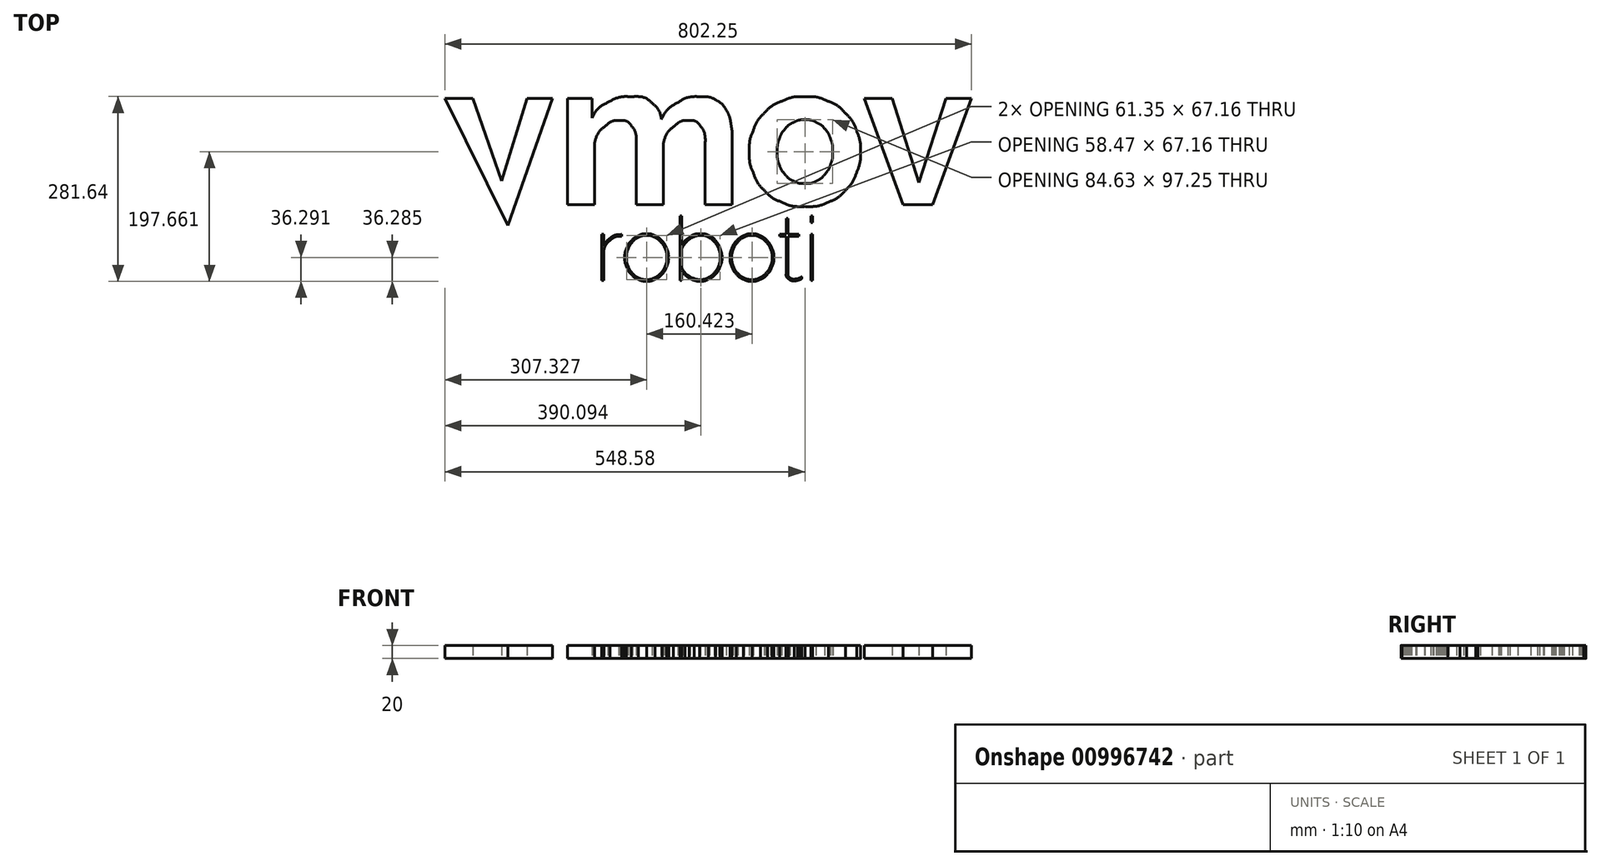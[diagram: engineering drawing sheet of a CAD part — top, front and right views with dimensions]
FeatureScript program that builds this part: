
annotation { "Feature Type Name" : "Feature", "Feature Type Description" : "" }
export const myFeature = defineFeature(function(context is Context, id is Id, definition is map)
    precondition{}
    {
        {
            var Q0;
            Q0=qCreatedBy(makeId("Top.planeOp"),FACE);
            var sketch = newSketch(context, id + "F0", { "sketchPlane" : qUnion([Q0])});
            skLineSegment(sketch, "E0", {"start": v(-278.2, 23.95) * mm, "end": v(-293.61, -1.95) * mm});
            skLineSegment(sketch, "E1", {"start": v(-293.61, -1.95) * mm, "end": v(-278.2, 23.95) * mm});
            skLineSegment(sketch, "E2", {"start": v(-178, 93.62) * mm, "end": v(-161.36, 118.6) * mm});
            skLineSegment(sketch, "E3", {"start": v(-161.36, 118.6) * mm, "end": v(-178, 93.62) * mm});
            skLineSegment(sketch, "E4", {"start": v(-493.33, 15.32) * mm, "end": v(-528.78, 25.18) * mm});
            skLineSegment(sketch, "E5", {"start": v(-528.78, 25.18) * mm, "end": v(-493.33, 15.32) * mm});
            skLineSegment(sketch, "E6", {"start": v(-609.86, 43.68) * mm, "end": v(-485, 43.68) * mm});
            skLineSegment(sketch, "E7", {"start": v(-485, 43.68) * mm, "end": v(-609.86, 43.68) * mm});
            skLineSegment(sketch, "E8", {"start": v(-460.77, 119.82) * mm, "end": v(-448.13, 93.62) * mm});
            skLineSegment(sketch, "E9", {"start": v(-448.13, 93.62) * mm, "end": v(-460.77, 119.82) * mm});
            skLineSegment(sketch, "E10", {"start": v(-361.5, 78.52) * mm, "end": v(-361.5, 69.26) * mm});
            skLineSegment(sketch, "E11", {"start": v(-361.5, 69.26) * mm, "end": v(-361.5, 78.52) * mm});
            skLineSegment(sketch, "E12", {"start": v(-355.33, 2.06) * mm, "end": v(-354.41, -6.88) * mm});
            skLineSegment(sketch, "E13", {"start": v(-354.41, -6.88) * mm, "end": v(-355.33, 2.06) * mm});
            skLineSegment(sketch, "E14", {"start": v(-310.33, -23.84) * mm, "end": v(-310.33, 11.3) * mm});
            skLineSegment(sketch, "E15", {"start": v(-310.33, 11.3) * mm, "end": v(-310.33, -23.84) * mm});
            skLineSegment(sketch, "E16", {"start": v(-320.2, 23.64) * mm, "end": v(-320.2, 73.89) * mm});
            skLineSegment(sketch, "E17", {"start": v(-320.2, 73.89) * mm, "end": v(-320.2, 23.64) * mm});
            skLineSegment(sketch, "E18", {"start": v(75.43, 107.8) * mm, "end": v(75.43, 137.7) * mm});
            skLineSegment(sketch, "E19", {"start": v(75.43, 137.7) * mm, "end": v(38.13, 137.7) * mm});
            skLineSegment(sketch, "E20", {"start": v(38.13, 137.7) * mm, "end": v(38.13, -23.84) * mm});
            skLineSegment(sketch, "E21", {"start": v(38.13, -23.84) * mm, "end": v(79.44, -23.84) * mm});
            skLineSegment(sketch, "E22", {"start": v(79.44, -23.84) * mm, "end": v(79.44, 70.5) * mm});
            skLineSegment(sketch, "E23", {"start": v(79.44, 70.5) * mm, "end": v(75.43, 107.8) * mm});
            skLineSegment(sketch, "E24", {"start": v(142.94, 66.8) * mm, "end": v(142.94, -23.84) * mm});
            skLineSegment(sketch, "E25", {"start": v(142.94, -23.84) * mm, "end": v(184.25, -23.84) * mm});
            skLineSegment(sketch, "E26", {"start": v(184.25, -23.84) * mm, "end": v(184.25, 70.19) * mm});
            skLineSegment(sketch, "E27", {"start": v(184.25, 70.19) * mm, "end": v(142.94, 66.8) * mm});
            skLineSegment(sketch, "E28", {"start": v(247.76, 66.8) * mm, "end": v(247.76, -23.84) * mm});
            skLineSegment(sketch, "E29", {"start": v(247.76, -23.84) * mm, "end": v(289.07, -23.84) * mm});
            skLineSegment(sketch, "E30", {"start": v(289.07, -23.84) * mm, "end": v(289.07, 76.98) * mm});
            skLineSegment(sketch, "E31", {"start": v(289.07, 76.98) * mm, "end": v(247.76, 66.8) * mm});
            skLineSegment(sketch, "E32", {"start": v(-148.62, 137.7) * mm, "end": v(-84.8, -23.84) * mm});
            skLineSegment(sketch, "E33", {"start": v(-84.8, -23.84) * mm, "end": v(-148.62, 137.7) * mm});
            skLineSegment(sketch, "E34", {"start": v(-128.27, -55.28) * mm, "end": v(-128.27, -91.04) * mm});
            skLineSegment(sketch, "E35", {"start": v(-128.27, -91.04) * mm, "end": v(-128.27, -55.28) * mm});
            skLineSegment(sketch, "E36", {"start": v(-52.44, -55.9) * mm, "end": v(15.39, 137.7) * mm});
            skLineSegment(sketch, "E37", {"start": v(15.39, 137.7) * mm, "end": v(-23.46, 137.7) * mm});
            skLineSegment(sketch, "E38", {"start": v(-23.46, 137.7) * mm, "end": v(-62.3, 11.92) * mm});
            skLineSegment(sketch, "E39", {"start": v(-62.3, 11.92) * mm, "end": v(-106.08, 137.7) * mm});
            skLineSegment(sketch, "E40", {"start": v(-106.08, 137.7) * mm, "end": v(-148.62, 137.7) * mm});
            skLineSegment(sketch, "E41", {"start": v(-148.62, 137.7) * mm, "end": v(-52.44, -55.9) * mm});
            skLineSegment(sketch, "E42", {"start": v(489.94, 137.7) * mm, "end": v(549.44, -23.84) * mm});
            skLineSegment(sketch, "E43", {"start": v(549.44, -23.84) * mm, "end": v(594.14, -23.84) * mm});
            skLineSegment(sketch, "E44", {"start": v(594.14, -23.84) * mm, "end": v(653.63, 137.7) * mm});
            skLineSegment(sketch, "E45", {"start": v(653.63, 137.7) * mm, "end": v(614.8, 137.7) * mm});
            skLineSegment(sketch, "E46", {"start": v(614.8, 137.7) * mm, "end": v(573.48, 9.77) * mm});
            skLineSegment(sketch, "E47", {"start": v(573.48, 9.77) * mm, "end": v(532.48, 137.7) * mm});
            skLineSegment(sketch, "E48", {"start": v(532.48, 137.7) * mm, "end": v(489.94, 137.7) * mm});
            skLineSegment(sketch, "E49", {"start": v(-526.62, 70.5) * mm, "end": v(-610.47, 70.5) * mm});
            skLineSegment(sketch, "E50", {"start": v(-610.47, 70.5) * mm, "end": v(-526.62, 70.5) * mm});
            skLineSegment(sketch, "E51", {"start": v(-361.5, 47.07) * mm, "end": v(-361.5, 28.57) * mm});
            skLineSegment(sketch, "E52", {"start": v(-361.5, 28.57) * mm, "end": v(-361.5, 47.07) * mm});
            skLineSegment(sketch, "E53", {"start": v(209.55, -40.98) * mm, "end": v(209.55, -139.44) * mm});
            skLineSegment(sketch, "E54", {"start": v(209.55, -139.44) * mm, "end": v(212.24, -139.44) * mm});
            skLineSegment(sketch, "E55", {"start": v(212.24, -139.44) * mm, "end": v(212.24, -124.87) * mm});
            skLineSegment(sketch, "E56", {"start": v(212.24, -124.87) * mm, "end": v(209.55, -40.98) * mm});
            skLineSegment(sketch, "E57", {"start": v(212.24, -85.76) * mm, "end": v(212.24, -40.98) * mm});
            skLineSegment(sketch, "E58", {"start": v(212.24, -40.98) * mm, "end": v(209.55, -40.98) * mm});
            skLineSegment(sketch, "E59", {"start": v(209.55, -40.98) * mm, "end": v(212.24, -85.76) * mm});
            skLineSegment(sketch, "E60", {"start": v(408.7, -40.98) * mm, "end": v(408.7, -51.37) * mm});
            skLineSegment(sketch, "E61", {"start": v(408.7, -51.37) * mm, "end": v(411.4, -51.37) * mm});
            skLineSegment(sketch, "E62", {"start": v(411.4, -51.37) * mm, "end": v(411.4, -40.98) * mm});
            skLineSegment(sketch, "E63", {"start": v(411.4, -40.98) * mm, "end": v(408.7, -40.98) * mm});
            skLineSegment(sketch, "E64", {"start": v(371.21, -45.03) * mm, "end": v(371.21, -69.44) * mm});
            skLineSegment(sketch, "E65", {"start": v(371.21, -69.44) * mm, "end": v(361.1, -69.44) * mm});
            skLineSegment(sketch, "E66", {"start": v(361.1, -69.44) * mm, "end": v(361.1, -72.14) * mm});
            skLineSegment(sketch, "E67", {"start": v(361.1, -72.14) * mm, "end": v(371.21, -72.14) * mm});
            skLineSegment(sketch, "E68", {"start": v(371.21, -72.14) * mm, "end": v(371.21, -129.32) * mm});
            skLineSegment(sketch, "E69", {"start": v(371.21, -129.32) * mm, "end": v(371.21, -45.03) * mm});
            skLineSegment(sketch, "E70", {"start": v(395.08, -136.87) * mm, "end": v(396.16, -136.2) * mm});
            skLineSegment(sketch, "E71", {"start": v(396.16, -136.2) * mm, "end": v(394.68, -134.04) * mm});
            skLineSegment(sketch, "E72", {"start": v(394.68, -134.04) * mm, "end": v(395.08, -136.87) * mm});
            skLineSegment(sketch, "E73", {"start": v(373.9, -129.32) * mm, "end": v(373.9, -72.14) * mm});
            skLineSegment(sketch, "E74", {"start": v(373.9, -72.14) * mm, "end": v(390.77, -72.14) * mm});
            skLineSegment(sketch, "E75", {"start": v(390.77, -72.14) * mm, "end": v(390.77, -69.44) * mm});
            skLineSegment(sketch, "E76", {"start": v(390.77, -69.44) * mm, "end": v(373.9, -69.44) * mm});
            skLineSegment(sketch, "E77", {"start": v(373.9, -69.44) * mm, "end": v(373.9, -45.03) * mm});
            skLineSegment(sketch, "E78", {"start": v(373.9, -45.03) * mm, "end": v(371.21, -45.03) * mm});
            skLineSegment(sketch, "E79", {"start": v(371.21, -45.03) * mm, "end": v(373.9, -129.32) * mm});
            skLineSegment(sketch, "E80", {"start": v(489.82, -124.2) * mm, "end": v(487.12, -123.4) * mm});
            skLineSegment(sketch, "E81", {"start": v(487.12, -123.4) * mm, "end": v(489.82, -124.2) * mm});
            skLineSegment(sketch, "E82", {"start": v(486.18, -84.95) * mm, "end": v(488.88, -84) * mm});
            skLineSegment(sketch, "E83", {"start": v(488.88, -84) * mm, "end": v(486.18, -84.95) * mm});
            skLineSegment(sketch, "E84", {"start": v(502.11, -127.7) * mm, "end": v(500.09, -129.46) * mm});
            skLineSegment(sketch, "E85", {"start": v(500.09, -129.46) * mm, "end": v(502.11, -127.7) * mm});
            skLineSegment(sketch, "E86", {"start": v(548.37, -79.56) * mm, "end": v(550.8, -78.48) * mm});
            skLineSegment(sketch, "E87", {"start": v(550.8, -78.48) * mm, "end": v(548.37, -79.56) * mm});
            skLineSegment(sketch, "E88", {"start": v(90.48, -69.44) * mm, "end": v(90.48, -139.44) * mm});
            skLineSegment(sketch, "E89", {"start": v(90.48, -139.44) * mm, "end": v(93.18, -139.44) * mm});
            skLineSegment(sketch, "E90", {"start": v(93.18, -139.44) * mm, "end": v(93.18, -95.2) * mm});
            skLineSegment(sketch, "E91", {"start": v(93.18, -95.2) * mm, "end": v(90.48, -69.44) * mm});
            skLineSegment(sketch, "E92", {"start": v(120.42, -72.14) * mm, "end": v(120.42, -69.44) * mm});
            skLineSegment(sketch, "E93", {"start": v(120.42, -69.44) * mm, "end": v(120.42, -72.14) * mm});
            skLineSegment(sketch, "E94", {"start": v(93.18, -87.52) * mm, "end": v(93.18, -69.44) * mm});
            skLineSegment(sketch, "E95", {"start": v(93.18, -69.44) * mm, "end": v(90.48, -69.44) * mm});
            skLineSegment(sketch, "E96", {"start": v(90.48, -69.44) * mm, "end": v(90.48, -69.44) * mm});
            skLineSegment(sketch, "E97", {"start": v(90.48, -69.44) * mm, "end": v(93.18, -87.52) * mm});
            skLineSegment(sketch, "E98", {"start": v(408.7, -69.44) * mm, "end": v(408.7, -139.44) * mm});
            skLineSegment(sketch, "E99", {"start": v(408.7, -139.44) * mm, "end": v(411.4, -139.44) * mm});
            skLineSegment(sketch, "E100", {"start": v(411.4, -139.44) * mm, "end": v(411.4, -69.44) * mm});
            skLineSegment(sketch, "E101", {"start": v(411.4, -69.44) * mm, "end": v(408.7, -69.44) * mm});
            skLineSegment(sketch, "E102", {"start": v(212.24, -116.91) * mm, "end": v(212.24, -91.42) * mm});
            skLineSegment(sketch, "E103", {"start": v(212.24, -91.42) * mm, "end": v(212.24, -116.91) * mm});
            skFitSpline(sketch, "E104", {"points": [v(-224.56, 140.79) * mm, v(-233.8, 140.79) * mm, v(-242.13, 139.55) * mm, v(-249.84, 137.09) * mm]});
            skFitSpline(sketch, "E105", {"points": [v(-249.84, 137.09) * mm, v(-257.54, 134.62) * mm, v(-264.33, 130.92) * mm, v(-269.88, 126.3) * mm]});
            skFitSpline(sketch, "E106", {"points": [v(-269.88, 126.3) * mm, v(-275.73, 121.67) * mm, v(-280.36, 116.12) * mm, v(-283.44, 109.65) * mm]});
            skFitSpline(sketch, "E107", {"points": [v(-283.44, 109.65) * mm, v(-286.52, 102.87) * mm, v(-288.06, 95.47) * mm, v(-288.06, 87.45) * mm]});
            skFitSpline(sketch, "E108", {"points": [v(-288.06, 87.45) * mm, v(-288.06, 81.29) * mm, v(-287.14, 75.74) * mm, v(-284.98, 71.43) * mm]});
            skFitSpline(sketch, "E109", {"points": [v(-284.98, 71.43) * mm, v(-283.13, 67.1) * mm, v(-279.74, 63.1) * mm, v(-275.12, 59.71) * mm]});
            skFitSpline(sketch, "E110", {"points": [v(-275.12, 59.71) * mm, v(-270.8, 56.32) * mm, v(-264.64, 53.24) * mm, v(-257.24, 50.77) * mm]});
            skFitSpline(sketch, "E111", {"points": [v(-257.24, 50.77) * mm, v(-249.84, 48) * mm, v(-240.9, 45.22) * mm, v(-230.42, 42.45) * mm]});
            skFitSpline(sketch, "E112", {"points": [v(-230.42, 42.45) * mm, v(-218.08, 38.75) * mm, v(-208.83, 35.66) * mm, v(-203.29, 33.2) * mm]});
            skFitSpline(sketch, "E113", {"points": [v(-203.29, 33.2) * mm, v(-197.74, 30.42) * mm, v(-194.96, 26.1) * mm, v(-194.96, 20.56) * mm]});
            skFitSpline(sketch, "E114", {"points": [v(-194.96, 20.56) * mm, v(-194.96, 14.7) * mm, v(-197.43, 10.39) * mm, v(-202.05, 7.3) * mm]});
            skFitSpline(sketch, "E115", {"points": [v(-202.05, 7.3) * mm, v(-206.99, 4.22) * mm, v(-213.46, 2.68) * mm, v(-221.47, 2.68) * mm]});
            skFitSpline(sketch, "E116", {"points": [v(-221.47, 2.68) * mm, v(-230.72, 2.68) * mm, v(-240.28, 4.22) * mm, v(-249.53, 7.92) * mm]});
            skFitSpline(sketch, "E117", {"points": [v(-249.53, 7.92) * mm, v(-258.78, 11.62) * mm, v(-268.33, 16.86) * mm, v(-278.2, 23.95) * mm]});
            skFitSpline(sketch, "E118", {"points": [v(-293.61, -1.95) * mm, v(-284.36, -9.96) * mm, v(-273.27, -16.13) * mm, v(-260.32, -20.44) * mm]});
            skFitSpline(sketch, "E119", {"points": [v(-260.32, -20.44) * mm, v(-247.37, -24.76) * mm, v(-234.11, -26.92) * mm, v(-220.55, -26.92) * mm]});
            skFitSpline(sketch, "E120", {"points": [v(-220.55, -26.92) * mm, v(-200.51, -26.92) * mm, v(-184.48, -22.6) * mm, v(-172.77, -13.35) * mm]});
            skFitSpline(sketch, "E121", {"points": [v(-172.77, -13.35) * mm, v(-161.05, -4.1) * mm, v(-155.2, 8.23) * mm, v(-155.2, 24.26) * mm]});
            skFitSpline(sketch, "E122", {"points": [v(-155.2, 24.26) * mm, v(-155.2, 31.04) * mm, v(-156.43, 36.59) * mm, v(-158.9, 41.52) * mm]});
            skFitSpline(sketch, "E123", {"points": [v(-158.9, 41.52) * mm, v(-161.36, 46.45) * mm, v(-165.06, 50.77) * mm, v(-170, 54.47) * mm]});
            skFitSpline(sketch, "E124", {"points": [v(-170, 54.47) * mm, v(-174.93, 58.17) * mm, v(-181.4, 61.25) * mm, v(-189.41, 64.33) * mm]});
            skFitSpline(sketch, "E125", {"points": [v(-189.41, 64.33) * mm, v(-197.43, 67.1) * mm, v(-206.68, 69.88) * mm, v(-217.78, 72.97) * mm]});
            skFitSpline(sketch, "E126", {"points": [v(-217.78, 72.97) * mm, v(-223.94, 74.2) * mm, v(-228.87, 75.74) * mm, v(-232.88, 76.98) * mm]});
            skFitSpline(sketch, "E127", {"points": [v(-232.88, 76.98) * mm, v(-236.89, 78.2) * mm, v(-239.97, 79.75) * mm, v(-242.44, 81.29) * mm]});
            skFitSpline(sketch, "E128", {"points": [v(-242.44, 81.29) * mm, v(-244.9, 82.52) * mm, v(-246.75, 84.37) * mm, v(-247.99, 86.22) * mm]});
            skFitSpline(sketch, "E129", {"points": [v(-247.99, 86.22) * mm, v(-249.22, 88.07) * mm, v(-249.53, 90.23) * mm, v(-249.53, 93.3) * mm]});
            skFitSpline(sketch, "E130", {"points": [v(-249.53, 93.3) * mm, v(-249.53, 99.48) * mm, v(-247.37, 104.1) * mm, v(-242.44, 107.19) * mm]});
            skFitSpline(sketch, "E131", {"points": [v(-242.44, 107.19) * mm, v(-237.81, 109.96) * mm, v(-231.96, 111.5) * mm, v(-224.87, 111.5) * mm]});
            skFitSpline(sketch, "E132", {"points": [v(-224.87, 111.5) * mm, v(-217.47, 111.5) * mm, v(-209.76, 109.96) * mm, v(-202.05, 107.19) * mm]});
            skFitSpline(sketch, "E133", {"points": [v(-202.05, 107.19) * mm, v(-194.35, 104.1) * mm, v(-186.33, 99.79) * mm, v(-178, 93.62) * mm]});
            skFitSpline(sketch, "E134", {"points": [v(-161.36, 118.6) * mm, v(-170.3, 126.3) * mm, v(-180.17, 131.85) * mm, v(-190.65, 135.55) * mm]});
            skFitSpline(sketch, "E135", {"points": [v(-190.65, 135.55) * mm, v(-201.13, 138.94) * mm, v(-212.54, 140.79) * mm, v(-224.56, 140.79) * mm]});
            skFitSpline(sketch, "E136", {"points": [v(-568.24, 140.48) * mm, v(-581.5, 140.48) * mm, v(-593.52, 138.02) * mm, v(-604, 133.7) * mm]});
            skFitSpline(sketch, "E137", {"points": [v(-604, 133.7) * mm, v(-614.48, 129.08) * mm, v(-623.42, 122.9) * mm, v(-630.82, 115.2) * mm]});
            skFitSpline(sketch, "E138", {"points": [v(-630.82, 115.2) * mm, v(-638.22, 107.5) * mm, v(-644.08, 98.55) * mm, v(-647.78, 88.38) * mm]});
            skFitSpline(sketch, "E139", {"points": [v(-647.78, 88.38) * mm, v(-651.78, 78.2) * mm, v(-653.63, 67.42) * mm, v(-653.63, 56.01) * mm]});
            skFitSpline(sketch, "E140", {"points": [v(-653.63, 56.01) * mm, v(-653.63, 44.91) * mm, v(-651.78, 34.12) * mm, v(-647.78, 24.26) * mm]});
            skFitSpline(sketch, "E141", {"points": [v(-647.78, 24.26) * mm, v(-643.77, 14.09) * mm, v(-637.91, 5.14) * mm, v(-630.51, -2.25) * mm]});
            skFitSpline(sketch, "E142", {"points": [v(-630.51, -2.25) * mm, v(-623.11, -9.96) * mm, v(-614.17, -16.13) * mm, v(-603.7, -20.44) * mm]});
            skFitSpline(sketch, "E143", {"points": [v(-603.7, -20.44) * mm, v(-593.2, -24.76) * mm, v(-581.5, -26.92) * mm, v(-568.55, -26.92) * mm]});
            skFitSpline(sketch, "E144", {"points": [v(-568.55, -26.92) * mm, v(-550.67, -26.92) * mm, v(-534.94, -23.22) * mm, v(-522, -15.2) * mm]});
            skFitSpline(sketch, "E145", {"points": [v(-522, -15.2) * mm, v(-509.05, -7.19) * mm, v(-499.5, 2.99) * mm, v(-493.33, 15.32) * mm]});
            skFitSpline(sketch, "E146", {"points": [v(-528.78, 25.18) * mm, v(-531.55, 18.4) * mm, v(-536.49, 13.16) * mm, v(-543.89, 9.15) * mm]});
            skFitSpline(sketch, "E147", {"points": [v(-543.89, 9.15) * mm, v(-551.28, 5.14) * mm, v(-559, 3.3) * mm, v(-567, 3.3) * mm]});
            skFitSpline(sketch, "E148", {"points": [v(-567, 3.3) * mm, v(-572.56, 3.3) * mm, v(-577.48, 4.22) * mm, v(-582.42, 6.07) * mm]});
            skFitSpline(sketch, "E149", {"points": [v(-582.42, 6.07) * mm, v(-587.35, 7.92) * mm, v(-591.98, 10.39) * mm, v(-595.68, 14.09) * mm]});
            skFitSpline(sketch, "E150", {"points": [v(-595.68, 14.09) * mm, v(-599.68, 17.48) * mm, v(-602.76, 21.8) * mm, v(-605.23, 26.72) * mm]});
            skFitSpline(sketch, "E151", {"points": [v(-605.23, 26.72) * mm, v(-607.7, 31.66) * mm, v(-609.24, 37.2) * mm, v(-609.86, 43.68) * mm]});
            skFitSpline(sketch, "E152", {"points": [v(-485, 43.68) * mm, v(-484.7, 45.22) * mm, v(-484.38, 47.38) * mm, v(-484.38, 49.84) * mm]});
            skFitSpline(sketch, "E153", {"points": [v(-484.38, 49.84) * mm, v(-484.38, 52.31) * mm, v(-484.08, 54.78) * mm, v(-484.08, 57.55) * mm]});
            skFitSpline(sketch, "E154", {"points": [v(-484.08, 57.55) * mm, v(-484.08, 68.34) * mm, v(-486.23, 78.82) * mm, v(-489.93, 89) * mm]});
            skFitSpline(sketch, "E155", {"points": [v(-489.93, 89) * mm, v(-493.63, 98.86) * mm, v(-499.18, 107.8) * mm, v(-506.58, 115.5) * mm]});
            skFitSpline(sketch, "E156", {"points": [v(-506.58, 115.5) * mm, v(-513.98, 122.9) * mm, v(-522.61, 129.08) * mm, v(-533.1, 133.7) * mm]});
            skFitSpline(sketch, "E157", {"points": [v(-533.1, 133.7) * mm, v(-543.58, 138.02) * mm, v(-555.3, 140.48) * mm, v(-568.24, 140.48) * mm]});
            skFitSpline(sketch, "E158", {"points": [v(-393.56, 140.48) * mm, v(-417.6, 140.48) * mm, v(-440.11, 133.39) * mm, v(-460.77, 119.82) * mm]});
            skFitSpline(sketch, "E159", {"points": [v(-448.13, 93.62) * mm, v(-439.5, 99.48) * mm, v(-431.17, 104.1) * mm, v(-422.85, 107.19) * mm]});
            skFitSpline(sketch, "E160", {"points": [v(-422.85, 107.19) * mm, v(-414.83, 110.27) * mm, v(-406.2, 111.81) * mm, v(-397.57, 111.81) * mm]});
            skFitSpline(sketch, "E161", {"points": [v(-397.57, 111.81) * mm, v(-385.86, 111.81) * mm, v(-376.92, 108.72) * mm, v(-370.75, 103.18) * mm]});
            skFitSpline(sketch, "E162", {"points": [v(-370.75, 103.18) * mm, v(-364.58, 97.32) * mm, v(-361.5, 89) * mm, v(-361.5, 78.52) * mm]});
            skFitSpline(sketch, "E163", {"points": [v(-361.5, 69.26) * mm, v(-367.05, 71.42) * mm, v(-373.22, 73.27) * mm, v(-380, 74.5) * mm]});
            skFitSpline(sketch, "E164", {"points": [v(-380, 74.5) * mm, v(-386.78, 75.74) * mm, v(-393.87, 76.36) * mm, v(-400.96, 76.36) * mm]});
            skFitSpline(sketch, "E165", {"points": [v(-400.96, 76.36) * mm, v(-411.13, 76.36) * mm, v(-420.38, 74.82) * mm, v(-428.7, 72.35) * mm]});
            skFitSpline(sketch, "E166", {"points": [v(-428.7, 72.35) * mm, v(-437.34, 69.88) * mm, v(-444.43, 66.18) * mm, v(-450.6, 61.87) * mm]});
            skFitSpline(sketch, "E167", {"points": [v(-450.6, 61.87) * mm, v(-456.76, 57.24) * mm, v(-461.38, 51.7) * mm, v(-464.77, 45.22) * mm]});
            skFitSpline(sketch, "E168", {"points": [v(-464.77, 45.22) * mm, v(-468.16, 38.75) * mm, v(-469.7, 31.66) * mm, v(-469.7, 24.26) * mm]});
            skFitSpline(sketch, "E169", {"points": [v(-469.7, 24.26) * mm, v(-469.7, 16.86) * mm, v(-468.48, 10.08) * mm, v(-465.7, 3.91) * mm]});
            skFitSpline(sketch, "E170", {"points": [v(-465.7, 3.91) * mm, v(-462.93, -2.25) * mm, v(-458.92, -7.8) * mm, v(-453.99, -12.43) * mm]});
            skFitSpline(sketch, "E171", {"points": [v(-453.99, -12.43) * mm, v(-449.06, -17.05) * mm, v(-443.2, -20.75) * mm, v(-436.42, -23.22) * mm]});
            skFitSpline(sketch, "E172", {"points": [v(-436.42, -23.22) * mm, v(-429.63, -25.69) * mm, v(-422.54, -26.92) * mm, v(-414.53, -26.92) * mm]});
            skFitSpline(sketch, "E173", {"points": [v(-414.53, -26.92) * mm, v(-402.81, -26.92) * mm, v(-392.02, -24.45) * mm, v(-381.54, -19.52) * mm]});
            skFitSpline(sketch, "E174", {"points": [v(-381.54, -19.52) * mm, v(-371.37, -14.59) * mm, v(-362.73, -7.5) * mm, v(-355.33, 2.06) * mm]});
            skFitSpline(sketch, "E175", {"points": [v(-354.41, -6.88) * mm, v(-353.49, -12.74) * mm, v(-351.02, -17.36) * mm, v(-346.7, -20.75) * mm]});
            skFitSpline(sketch, "E176", {"points": [v(-346.7, -20.75) * mm, v(-342.39, -24.45) * mm, v(-336.53, -26) * mm, v(-328.52, -26) * mm]});
            skFitSpline(sketch, "E177", {"points": [v(-328.52, -26) * mm, v(-323.58, -26) * mm, v(-317.42, -25.38) * mm, v(-310.33, -23.84) * mm]});
            skFitSpline(sketch, "E178", {"points": [v(-310.33, 11.3) * mm, v(-314.03, 11.3) * mm, v(-316.5, 12.54) * mm, v(-318.03, 14.4) * mm]});
            skFitSpline(sketch, "E179", {"points": [v(-318.03, 14.4) * mm, v(-319.58, 16.24) * mm, v(-320.2, 19.32) * mm, v(-320.2, 23.64) * mm]});
            skFitSpline(sketch, "E180", {"points": [v(-320.2, 73.89) * mm, v(-320.2, 95.47) * mm, v(-326.67, 111.81) * mm, v(-339.62, 123.22) * mm]});
            skFitSpline(sketch, "E181", {"points": [v(-339.62, 123.22) * mm, v(-352.56, 134.62) * mm, v(-370.44, 140.48) * mm, v(-393.56, 140.48) * mm]});
            skFitSpline(sketch, "E182", {"points": [v(135.55, 140.48) * mm, v(121.98, 140.48) * mm, v(110.27, 137.4) * mm, v(99.79, 131.85) * mm]});
            skFitSpline(sketch, "E183", {"points": [v(99.79, 131.85) * mm, v(89.3, 126.3) * mm, v(81.29, 118.28) * mm, v(75.43, 107.8) * mm]});
            skFitSpline(sketch, "E184", {"points": [v(79.44, 70.5) * mm, v(82.52, 80.37) * mm, v(87.46, 88.69) * mm, v(94.85, 94.85) * mm]});
            skFitSpline(sketch, "E185", {"points": [v(94.85, 94.85) * mm, v(102.25, 101.02) * mm, v(109.96, 104.1) * mm, v(117.98, 104.1) * mm]});
            skFitSpline(sketch, "E186", {"points": [v(117.98, 104.1) * mm, v(125.68, 104.1) * mm, v(131.85, 101.02) * mm, v(136.16, 95.16) * mm]});
            skFitSpline(sketch, "E187", {"points": [v(136.16, 95.16) * mm, v(140.48, 89) * mm, v(142.94, 79.75) * mm, v(142.94, 66.8) * mm]});
            skFitSpline(sketch, "E188", {"points": [v(184.25, 70.19) * mm, v(187.34, 80.05) * mm, v(192.27, 88.38) * mm, v(199.67, 94.55) * mm]});
            skFitSpline(sketch, "E189", {"points": [v(199.67, 94.55) * mm, v(206.76, 100.71) * mm, v(214.47, 104.1) * mm, v(222.79, 104.1) * mm]});
            skFitSpline(sketch, "E190", {"points": [v(222.79, 104.1) * mm, v(230.5, 104.1) * mm, v(236.66, 101.02) * mm, v(240.98, 95.16) * mm]});
            skFitSpline(sketch, "E191", {"points": [v(240.98, 95.16) * mm, v(245.3, 89) * mm, v(247.76, 79.75) * mm, v(247.76, 66.8) * mm]});
            skFitSpline(sketch, "E192", {"points": [v(289.07, 76.98) * mm, v(289.07, 84.68) * mm, v(288.14, 92.39) * mm, v(286.91, 100.1) * mm]});
            skFitSpline(sketch, "E193", {"points": [v(286.91, 100.1) * mm, v(285.68, 107.5) * mm, v(283.21, 114.27) * mm, v(279.82, 120.44) * mm]});
            skFitSpline(sketch, "E194", {"points": [v(279.82, 120.44) * mm, v(276.12, 126.3) * mm, v(271.19, 131.23) * mm, v(265.02, 134.93) * mm]});
            skFitSpline(sketch, "E195", {"points": [v(265.02, 134.93) * mm, v(258.55, 138.63) * mm, v(250.53, 140.48) * mm, v(240.67, 140.48) * mm]});
            skFitSpline(sketch, "E196", {"points": [v(240.67, 140.48) * mm, v(227.72, 140.48) * mm, v(216, 137.4) * mm, v(206.14, 131.54) * mm]});
            skFitSpline(sketch, "E197", {"points": [v(206.14, 131.54) * mm, v(195.97, 125.68) * mm, v(187.65, 117.36) * mm, v(181.17, 106.26) * mm]});
            skFitSpline(sketch, "E198", {"points": [v(181.17, 106.26) * mm, v(179.02, 115.82) * mm, v(174.39, 123.83) * mm, v(166.99, 130.61) * mm]});
            skFitSpline(sketch, "E199", {"points": [v(166.99, 130.61) * mm, v(159.6, 137.09) * mm, v(149.11, 140.48) * mm, v(135.55, 140.48) * mm]});
            skFitSpline(sketch, "E200", {"points": [v(399.94, 140.48) * mm, v(386.68, 140.48) * mm, v(374.97, 138.02) * mm, v(364.49, 133.7) * mm]});
            skFitSpline(sketch, "E201", {"points": [v(364.49, 133.7) * mm, v(354, 129.08) * mm, v(345.07, 122.9) * mm, v(337.67, 115.2) * mm]});
            skFitSpline(sketch, "E202", {"points": [v(337.67, 115.2) * mm, v(330.27, 107.5) * mm, v(324.72, 98.55) * mm, v(321.02, 88.69) * mm]});
            skFitSpline(sketch, "E203", {"points": [v(321.02, 88.69) * mm, v(317.01, 78.52) * mm, v(315.16, 67.72) * mm, v(315.16, 56.63) * mm]});
            skFitSpline(sketch, "E204", {"points": [v(315.16, 56.63) * mm, v(315.16, 45.53) * mm, v(317.01, 34.74) * mm, v(321.02, 24.88) * mm]});
            skFitSpline(sketch, "E205", {"points": [v(321.02, 24.88) * mm, v(324.72, 14.7) * mm, v(330.27, 5.76) * mm, v(337.67, -1.95) * mm]});
            skFitSpline(sketch, "E206", {"points": [v(337.67, -1.95) * mm, v(345.07, -9.65) * mm, v(354, -15.82) * mm, v(364.49, -20.13) * mm]});
            skFitSpline(sketch, "E207", {"points": [v(364.49, -20.13) * mm, v(374.97, -24.76) * mm, v(386.68, -26.92) * mm, v(399.94, -26.92) * mm]});
            skFitSpline(sketch, "E208", {"points": [v(399.94, -26.92) * mm, v(412.89, -26.92) * mm, v(424.91, -24.76) * mm, v(435.4, -20.13) * mm]});
            skFitSpline(sketch, "E209", {"points": [v(435.4, -20.13) * mm, v(445.87, -15.82) * mm, v(454.5, -9.65) * mm, v(461.9, -1.95) * mm]});
            skFitSpline(sketch, "E210", {"points": [v(461.9, -1.95) * mm, v(469, 5.76) * mm, v(474.55, 14.7) * mm, v(478.55, 24.88) * mm]});
            skFitSpline(sketch, "E211", {"points": [v(478.55, 24.88) * mm, v(482.25, 34.74) * mm, v(484.41, 45.53) * mm, v(484.41, 56.63) * mm]});
            skFitSpline(sketch, "E212", {"points": [v(484.41, 56.63) * mm, v(484.41, 67.72) * mm, v(482.25, 78.52) * mm, v(478.55, 88.69) * mm]});
            skFitSpline(sketch, "E213", {"points": [v(478.55, 88.69) * mm, v(474.55, 98.55) * mm, v(469, 107.5) * mm, v(461.6, 115.2) * mm]});
            skFitSpline(sketch, "E214", {"points": [v(461.6, 115.2) * mm, v(454.2, 122.9) * mm, v(445.57, 129.08) * mm, v(435.08, 133.7) * mm]});
            skFitSpline(sketch, "E215", {"points": [v(435.08, 133.7) * mm, v(424.6, 138.02) * mm, v(412.89, 140.48) * mm, v(399.94, 140.48) * mm]});
            skFitSpline(sketch, "E216", {"points": [v(-84.8, -23.84) * mm, v(-86.97, -30.62) * mm, v(-88.82, -36.47) * mm, v(-90.66, -40.8) * mm]});
            skFitSpline(sketch, "E217", {"points": [v(-90.66, -40.8) * mm, v(-92.51, -45.42) * mm, v(-94.36, -49.12) * mm, v(-96.21, -51.58) * mm]});
            skFitSpline(sketch, "E218", {"points": [v(-96.21, -51.58) * mm, v(-98.06, -54.05) * mm, v(-100.22, -55.9) * mm, v(-102.38, -56.82) * mm]});
            skFitSpline(sketch, "E219", {"points": [v(-102.38, -56.82) * mm, v(-104.85, -58.06) * mm, v(-107.31, -58.36) * mm, v(-109.78, -58.36) * mm]});
            skFitSpline(sketch, "E220", {"points": [v(-109.78, -58.36) * mm, v(-112.24, -58.36) * mm, v(-115.02, -58.36) * mm, v(-118.1, -57.75) * mm]});
            skFitSpline(sketch, "E221", {"points": [v(-118.1, -57.75) * mm, v(-121.49, -57.13) * mm, v(-124.88, -56.51) * mm, v(-128.27, -55.28) * mm]});
            skFitSpline(sketch, "E222", {"points": [v(-128.27, -91.04) * mm, v(-124.57, -92.28) * mm, v(-121.18, -93.2) * mm, v(-117.79, -93.81) * mm]});
            skFitSpline(sketch, "E223", {"points": [v(-117.79, -93.81) * mm, v(-114.4, -94.43) * mm, v(-111.01, -94.43) * mm, v(-107.62, -94.43) * mm]});
            skFitSpline(sketch, "E224", {"points": [v(-107.62, -94.43) * mm, v(-93.75, -94.43) * mm, v(-82.03, -91.04) * mm, v(-72.48, -83.64) * mm]});
            skFitSpline(sketch, "E225", {"points": [v(-72.48, -83.64) * mm, v(-63.23, -76.55) * mm, v(-56.44, -67.3) * mm, v(-52.44, -55.9) * mm]});
            skFitSpline(sketch, "E226", {"points": [v(-568.85, 110.57) * mm, v(-557.76, 110.57) * mm, v(-548.2, 106.88) * mm, v(-540.18, 99.48) * mm]});
            skFitSpline(sketch, "E227", {"points": [v(-540.18, 99.48) * mm, v(-532.17, 92.08) * mm, v(-527.86, 82.52) * mm, v(-526.62, 70.5) * mm]});
            skFitSpline(sketch, "E228", {"points": [v(-610.47, 70.5) * mm, v(-610.16, 76.36) * mm, v(-608.93, 81.9) * mm, v(-606.46, 86.84) * mm]});
            skFitSpline(sketch, "E229", {"points": [v(-606.46, 86.84) * mm, v(-604, 91.77) * mm, v(-600.92, 95.78) * mm, v(-597.22, 99.48) * mm]});
            skFitSpline(sketch, "E230", {"points": [v(-597.22, 99.48) * mm, v(-593.52, 102.87) * mm, v(-589.51, 105.64) * mm, v(-584.58, 107.5) * mm]});
            skFitSpline(sketch, "E231", {"points": [v(-584.58, 107.5) * mm, v(-579.65, 109.34) * mm, v(-574.4, 110.57) * mm, v(-568.85, 110.57) * mm]});
            skFitSpline(sketch, "E232", {"points": [v(399.94, 105.34) * mm, v(405.8, 105.34) * mm, v(411.35, 104.1) * mm, v(416.59, 101.64) * mm]});
            skFitSpline(sketch, "E233", {"points": [v(416.59, 101.64) * mm, v(421.52, 99.17) * mm, v(426.14, 96.09) * mm, v(429.84, 91.77) * mm]});
            skFitSpline(sketch, "E234", {"points": [v(429.84, 91.77) * mm, v(433.54, 87.45) * mm, v(436.63, 82.22) * mm, v(438.79, 76.36) * mm]});
            skFitSpline(sketch, "E235", {"points": [v(438.79, 76.36) * mm, v(440.94, 70.2) * mm, v(442.17, 63.72) * mm, v(442.17, 56.93) * mm]});
            skFitSpline(sketch, "E236", {"points": [v(442.17, 56.93) * mm, v(442.17, 49.54) * mm, v(440.94, 43.06) * mm, v(438.79, 37.2) * mm]});
            skFitSpline(sketch, "E237", {"points": [v(438.79, 37.2) * mm, v(436.63, 31.04) * mm, v(433.54, 26.1) * mm, v(429.84, 21.8) * mm]});
            skFitSpline(sketch, "E238", {"points": [v(429.84, 21.8) * mm, v(426.14, 17.47) * mm, v(421.52, 14.08) * mm, v(416.59, 11.62) * mm]});
            skFitSpline(sketch, "E239", {"points": [v(416.59, 11.62) * mm, v(411.35, 9.15) * mm, v(405.8, 8.23) * mm, v(399.94, 8.23) * mm]});
            skFitSpline(sketch, "E240", {"points": [v(399.94, 8.23) * mm, v(393.77, 8.23) * mm, v(388.23, 9.15) * mm, v(383.3, 11.62) * mm]});
            skFitSpline(sketch, "E241", {"points": [v(383.3, 11.62) * mm, v(378.05, 14.08) * mm, v(373.43, 17.47) * mm, v(369.73, 21.8) * mm]});
            skFitSpline(sketch, "E242", {"points": [v(369.73, 21.8) * mm, v(366.03, 26.1) * mm, v(362.95, 31.04) * mm, v(360.79, 36.9) * mm]});
            skFitSpline(sketch, "E243", {"points": [v(360.79, 36.9) * mm, v(358.63, 42.76) * mm, v(357.7, 49.23) * mm, v(357.7, 56.63) * mm]});
            skFitSpline(sketch, "E244", {"points": [v(357.7, 56.63) * mm, v(357.7, 63.4) * mm, v(358.63, 69.88) * mm, v(360.79, 76.05) * mm]});
            skFitSpline(sketch, "E245", {"points": [v(360.79, 76.05) * mm, v(362.95, 81.9) * mm, v(366.03, 87.15) * mm, v(369.73, 91.46) * mm]});
            skFitSpline(sketch, "E246", {"points": [v(369.73, 91.46) * mm, v(373.43, 95.78) * mm, v(378.05, 99.17) * mm, v(383.3, 101.64) * mm]});
            skFitSpline(sketch, "E247", {"points": [v(383.3, 101.64) * mm, v(388.23, 104.1) * mm, v(393.77, 105.34) * mm, v(399.94, 105.34) * mm]});
            skFitSpline(sketch, "E248", {"points": [v(-394.18, 53.24) * mm, v(-388.94, 53.24) * mm, v(-383.39, 52.62) * mm, v(-377.53, 51.38) * mm]});
            skFitSpline(sketch, "E249", {"points": [v(-377.53, 51.38) * mm, v(-371.98, 50.15) * mm, v(-366.43, 48.92) * mm, v(-361.5, 47.07) * mm]});
            skFitSpline(sketch, "E250", {"points": [v(-361.5, 28.57) * mm, v(-361.5, 24.26) * mm, v(-363.97, 20.25) * mm, v(-368.29, 16.86) * mm]});
            skFitSpline(sketch, "E251", {"points": [v(-368.29, 16.86) * mm, v(-371.99, 12.54) * mm, v(-376.91, 9.46) * mm, v(-383.08, 7) * mm]});
            skFitSpline(sketch, "E252", {"points": [v(-383.08, 7) * mm, v(-389.25, 4.53) * mm, v(-396.03, 3.3) * mm, v(-402.81, 3.3) * mm]});
            skFitSpline(sketch, "E253", {"points": [v(-402.81, 3.3) * mm, v(-410.83, 3.3) * mm, v(-417.3, 5.45) * mm, v(-422.54, 10.08) * mm]});
            skFitSpline(sketch, "E254", {"points": [v(-422.54, 10.08) * mm, v(-428.1, 14.7) * mm, v(-430.55, 20.56) * mm, v(-430.55, 27.65) * mm]});
            skFitSpline(sketch, "E255", {"points": [v(-430.55, 27.65) * mm, v(-430.55, 35.05) * mm, v(-427.17, 40.9) * mm, v(-420.39, 45.84) * mm]});
            skFitSpline(sketch, "E256", {"points": [v(-420.39, 45.84) * mm, v(-413.6, 50.77) * mm, v(-404.97, 53.24) * mm, v(-394.18, 53.24) * mm]});
            skFitSpline(sketch, "E257", {"points": [v(212.24, -124.87) * mm, v(213.6, -127.17) * mm, v(215.21, -129.33) * mm, v(217.24, -131.21) * mm]});
            skFitSpline(sketch, "E258", {"points": [v(217.24, -131.21) * mm, v(219.26, -133.1) * mm, v(221.41, -134.85) * mm, v(223.84, -136.2) * mm]});
            skFitSpline(sketch, "E259", {"points": [v(223.84, -136.2) * mm, v(226.27, -137.68) * mm, v(228.7, -138.76) * mm, v(231.4, -139.57) * mm]});
            skFitSpline(sketch, "E260", {"points": [v(231.4, -139.57) * mm, v(234.1, -140.38) * mm, v(236.8, -140.79) * mm, v(239.62, -140.79) * mm]});
            skFitSpline(sketch, "E261", {"points": [v(239.62, -140.79) * mm, v(244.34, -140.79) * mm, v(248.8, -139.84) * mm, v(252.84, -137.82) * mm]});
            skFitSpline(sketch, "E262", {"points": [v(252.84, -137.82) * mm, v(256.89, -135.93) * mm, v(260.53, -133.24) * mm, v(263.63, -129.87) * mm]});
            skFitSpline(sketch, "E263", {"points": [v(263.63, -129.87) * mm, v(266.6, -126.63) * mm, v(269.03, -122.72) * mm, v(270.78, -118.4) * mm]});
            skFitSpline(sketch, "E264", {"points": [v(270.78, -118.4) * mm, v(272.4, -114.08) * mm, v(273.34, -109.5) * mm, v(273.34, -104.64) * mm]});
            skFitSpline(sketch, "E265", {"points": [v(273.34, -104.64) * mm, v(273.34, -100.33) * mm, v(272.53, -96.01) * mm, v(271.05, -91.7) * mm]});
            skFitSpline(sketch, "E266", {"points": [v(271.05, -91.7) * mm, v(269.57, -87.38) * mm, v(267.4, -83.6) * mm, v(264.7, -80.1) * mm]});
            skFitSpline(sketch, "E267", {"points": [v(264.7, -80.1) * mm, v(262.01, -76.6) * mm, v(258.64, -73.76) * mm, v(254.6, -71.6) * mm]});
            skFitSpline(sketch, "E268", {"points": [v(254.6, -71.6) * mm, v(250.55, -69.44) * mm, v(245.96, -68.36) * mm, v(240.84, -68.36) * mm]});
            skFitSpline(sketch, "E269", {"points": [v(240.84, -68.36) * mm, v(234.64, -68.36) * mm, v(229.24, -70.12) * mm, v(224.65, -73.35) * mm]});
            skFitSpline(sketch, "E270", {"points": [v(224.65, -73.35) * mm, v(219.93, -76.6) * mm, v(215.75, -80.77) * mm, v(212.24, -85.76) * mm]});
            skFitSpline(sketch, "E271", {"points": [v(371.21, -129.32) * mm, v(371.21, -132.56) * mm, v(372.43, -135.26) * mm, v(374.85, -137.15) * mm]});
            skFitSpline(sketch, "E272", {"points": [v(374.85, -137.15) * mm, v(377.28, -139.17) * mm, v(380.11, -140.11) * mm, v(383.35, -140.11) * mm]});
            skFitSpline(sketch, "E273", {"points": [v(383.35, -140.11) * mm, v(385.24, -140.11) * mm, v(386.86, -139.98) * mm, v(388.48, -139.57) * mm]});
            skFitSpline(sketch, "E274", {"points": [v(388.48, -139.57) * mm, v(389.96, -139.17) * mm, v(391.3, -138.76) * mm, v(392.38, -138.22) * mm]});
            skFitSpline(sketch, "E275", {"points": [v(392.38, -138.22) * mm, v(393.46, -137.82) * mm, v(394.4, -137.41) * mm, v(395.08, -136.87) * mm]});
            skFitSpline(sketch, "E276", {"points": [v(394.68, -134.04) * mm, v(394.54, -134.18) * mm, v(394.14, -134.45) * mm, v(393.6, -134.72) * mm]});
            skFitSpline(sketch, "E277", {"points": [v(393.6, -134.72) * mm, v(393.06, -135.12) * mm, v(392.25, -135.53) * mm, v(391.17, -135.93) * mm]});
            skFitSpline(sketch, "E278", {"points": [v(391.17, -135.93) * mm, v(390.1, -136.34) * mm, v(389.01, -136.74) * mm, v(387.66, -137.01) * mm]});
            skFitSpline(sketch, "E279", {"points": [v(387.66, -137.01) * mm, v(386.31, -137.28) * mm, v(384.83, -137.42) * mm, v(383.35, -137.42) * mm]});
            skFitSpline(sketch, "E280", {"points": [v(383.35, -137.42) * mm, v(380.92, -137.42) * mm, v(378.9, -136.74) * mm, v(377.01, -135.4) * mm]});
            skFitSpline(sketch, "E281", {"points": [v(377.01, -135.4) * mm, v(375.12, -134.04) * mm, v(374.04, -132.02) * mm, v(373.9, -129.32) * mm]});
            skFitSpline(sketch, "E282", {"points": [v(158.71, -68.36) * mm, v(154.13, -68.36) * mm, v(149.94, -69.44) * mm, v(145.9, -71.33) * mm]});
            skFitSpline(sketch, "E283", {"points": [v(145.9, -71.33) * mm, v(141.85, -73.22) * mm, v(138.2, -75.92) * mm, v(135.24, -79.15) * mm]});
            skFitSpline(sketch, "E284", {"points": [v(135.24, -79.15) * mm, v(132.14, -82.52) * mm, v(129.71, -86.43) * mm, v(127.96, -90.75) * mm]});
            skFitSpline(sketch, "E285", {"points": [v(127.96, -90.75) * mm, v(126.2, -95.07) * mm, v(125.4, -99.79) * mm, v(125.4, -104.64) * mm]});
            skFitSpline(sketch, "E286", {"points": [v(125.4, -104.64) * mm, v(125.4, -109.5) * mm, v(126.2, -114.22) * mm, v(127.96, -118.53) * mm]});
            skFitSpline(sketch, "E287", {"points": [v(127.96, -118.53) * mm, v(129.71, -122.98) * mm, v(132.14, -126.9) * mm, v(135.1, -130.13) * mm]});
            skFitSpline(sketch, "E288", {"points": [v(135.1, -130.13) * mm, v(138.07, -133.37) * mm, v(141.71, -136.07) * mm, v(145.76, -137.96) * mm]});
            skFitSpline(sketch, "E289", {"points": [v(145.76, -137.96) * mm, v(149.8, -139.85) * mm, v(154.13, -140.79) * mm, v(158.71, -140.79) * mm]});
            skFitSpline(sketch, "E290", {"points": [v(158.71, -140.79) * mm, v(163.3, -140.79) * mm, v(167.61, -139.85) * mm, v(171.66, -137.96) * mm]});
            skFitSpline(sketch, "E291", {"points": [v(171.66, -137.96) * mm, v(175.7, -136.07) * mm, v(179.2, -133.37) * mm, v(182.18, -130.13) * mm]});
            skFitSpline(sketch, "E292", {"points": [v(182.18, -130.13) * mm, v(185.14, -126.9) * mm, v(187.57, -122.98) * mm, v(189.32, -118.53) * mm]});
            skFitSpline(sketch, "E293", {"points": [v(189.32, -118.53) * mm, v(191.08, -114.22) * mm, v(192.02, -109.5) * mm, v(192.02, -104.64) * mm]});
            skFitSpline(sketch, "E294", {"points": [v(192.02, -104.64) * mm, v(192.02, -99.79) * mm, v(191.08, -95.07) * mm, v(189.32, -90.75) * mm]});
            skFitSpline(sketch, "E295", {"points": [v(189.32, -90.75) * mm, v(187.44, -86.43) * mm, v(185.01, -82.52) * mm, v(182.04, -79.15) * mm]});
            skFitSpline(sketch, "E296", {"points": [v(182.04, -79.15) * mm, v(179.08, -75.92) * mm, v(175.57, -73.22) * mm, v(171.52, -71.33) * mm]});
            skFitSpline(sketch, "E297", {"points": [v(171.52, -71.33) * mm, v(167.47, -69.44) * mm, v(163.16, -68.36) * mm, v(158.71, -68.36) * mm]});
            skFitSpline(sketch, "E298", {"points": [v(319.13, -68.36) * mm, v(314.55, -68.36) * mm, v(310.37, -69.44) * mm, v(306.32, -71.33) * mm]});
            skFitSpline(sketch, "E299", {"points": [v(306.32, -71.33) * mm, v(302.27, -73.22) * mm, v(298.64, -75.92) * mm, v(295.67, -79.15) * mm]});
            skFitSpline(sketch, "E300", {"points": [v(295.67, -79.15) * mm, v(292.57, -82.52) * mm, v(290.14, -86.43) * mm, v(288.38, -90.75) * mm]});
            skFitSpline(sketch, "E301", {"points": [v(288.38, -90.75) * mm, v(286.63, -95.07) * mm, v(285.82, -99.79) * mm, v(285.82, -104.64) * mm]});
            skFitSpline(sketch, "E302", {"points": [v(285.82, -104.64) * mm, v(285.82, -109.5) * mm, v(286.63, -114.22) * mm, v(288.38, -118.53) * mm]});
            skFitSpline(sketch, "E303", {"points": [v(288.38, -118.53) * mm, v(290.14, -122.98) * mm, v(292.56, -126.9) * mm, v(295.53, -130.13) * mm]});
            skFitSpline(sketch, "E304", {"points": [v(295.53, -130.13) * mm, v(298.5, -133.37) * mm, v(302.14, -136.07) * mm, v(306.19, -137.96) * mm]});
            skFitSpline(sketch, "E305", {"points": [v(306.19, -137.96) * mm, v(310.23, -139.85) * mm, v(314.55, -140.79) * mm, v(319.13, -140.79) * mm]});
            skFitSpline(sketch, "E306", {"points": [v(319.13, -140.79) * mm, v(323.72, -140.79) * mm, v(328.03, -139.85) * mm, v(332.08, -137.96) * mm]});
            skFitSpline(sketch, "E307", {"points": [v(332.08, -137.96) * mm, v(336.13, -136.07) * mm, v(339.63, -133.37) * mm, v(342.6, -130.13) * mm]});
            skFitSpline(sketch, "E308", {"points": [v(342.6, -130.13) * mm, v(345.57, -126.9) * mm, v(348, -122.98) * mm, v(349.75, -118.53) * mm]});
            skFitSpline(sketch, "E309", {"points": [v(349.75, -118.53) * mm, v(351.5, -114.22) * mm, v(352.45, -109.5) * mm, v(352.45, -104.64) * mm]});
            skFitSpline(sketch, "E310", {"points": [v(352.45, -104.64) * mm, v(352.45, -99.79) * mm, v(351.5, -95.07) * mm, v(349.75, -90.75) * mm]});
            skFitSpline(sketch, "E311", {"points": [v(349.75, -90.75) * mm, v(347.86, -86.43) * mm, v(345.43, -82.52) * mm, v(342.47, -79.15) * mm]});
            skFitSpline(sketch, "E312", {"points": [v(342.47, -79.15) * mm, v(339.5, -75.92) * mm, v(336, -73.22) * mm, v(331.95, -71.33) * mm]});
            skFitSpline(sketch, "E313", {"points": [v(331.95, -71.33) * mm, v(327.9, -69.44) * mm, v(323.58, -68.36) * mm, v(319.13, -68.36) * mm]});
            skFitSpline(sketch, "E314", {"points": [v(462.58, -68.36) * mm, v(457.72, -68.36) * mm, v(453.27, -69.3) * mm, v(449.23, -71.2) * mm]});
            skFitSpline(sketch, "E315", {"points": [v(449.23, -71.2) * mm, v(445.18, -73.08) * mm, v(441.53, -75.51) * mm, v(438.57, -78.75) * mm]});
            skFitSpline(sketch, "E316", {"points": [v(438.57, -78.75) * mm, v(435.47, -81.99) * mm, v(433.04, -85.76) * mm, v(431.42, -90.08) * mm]});
            skFitSpline(sketch, "E317", {"points": [v(431.42, -90.08) * mm, v(429.67, -94.4) * mm, v(428.86, -99.11) * mm, v(428.86, -104.1) * mm]});
            skFitSpline(sketch, "E318", {"points": [v(428.86, -104.1) * mm, v(428.86, -109.23) * mm, v(429.67, -113.95) * mm, v(431.56, -118.4) * mm]});
            skFitSpline(sketch, "E319", {"points": [v(431.56, -118.4) * mm, v(433.31, -122.85) * mm, v(435.74, -126.76) * mm, v(438.84, -130) * mm]});
            skFitSpline(sketch, "E320", {"points": [v(438.84, -130) * mm, v(441.8, -133.37) * mm, v(445.45, -136.07) * mm, v(449.63, -137.96) * mm]});
            skFitSpline(sketch, "E321", {"points": [v(449.63, -137.96) * mm, v(453.67, -139.85) * mm, v(458.13, -140.79) * mm, v(462.71, -140.79) * mm]});
            skFitSpline(sketch, "E322", {"points": [v(462.71, -140.79) * mm, v(465.68, -140.79) * mm, v(468.65, -140.38) * mm, v(471.61, -139.57) * mm]});
            skFitSpline(sketch, "E323", {"points": [v(471.61, -139.57) * mm, v(474.58, -138.76) * mm, v(477.28, -137.55) * mm, v(479.7, -136.07) * mm]});
            skFitSpline(sketch, "E324", {"points": [v(479.7, -136.07) * mm, v(482.13, -134.58) * mm, v(484.16, -132.83) * mm, v(485.9, -130.8) * mm]});
            skFitSpline(sketch, "E325", {"points": [v(485.9, -130.8) * mm, v(487.66, -128.78) * mm, v(489.01, -126.63) * mm, v(489.82, -124.2) * mm]});
            skFitSpline(sketch, "E326", {"points": [v(487.12, -123.4) * mm, v(486.59, -125.28) * mm, v(485.5, -127.17) * mm, v(483.89, -128.92) * mm]});
            skFitSpline(sketch, "E327", {"points": [v(483.89, -128.92) * mm, v(482.27, -130.8) * mm, v(480.25, -132.3) * mm, v(477.95, -133.64) * mm]});
            skFitSpline(sketch, "E328", {"points": [v(477.95, -133.64) * mm, v(475.66, -134.99) * mm, v(473.1, -136.07) * mm, v(470.4, -136.87) * mm]});
            skFitSpline(sketch, "E329", {"points": [v(470.4, -136.87) * mm, v(467.7, -137.68) * mm, v(465, -138.1) * mm, v(462.3, -138.1) * mm]});
            skFitSpline(sketch, "E330", {"points": [v(462.3, -138.1) * mm, v(457.99, -138.1) * mm, v(454.08, -137.28) * mm, v(450.44, -135.4) * mm]});
            skFitSpline(sketch, "E331", {"points": [v(450.44, -135.4) * mm, v(446.66, -133.64) * mm, v(443.42, -131.2) * mm, v(440.6, -128.1) * mm]});
            skFitSpline(sketch, "E332", {"points": [v(440.6, -128.1) * mm, v(437.76, -125) * mm, v(435.6, -121.37) * mm, v(433.98, -117.18) * mm]});
            skFitSpline(sketch, "E333", {"points": [v(433.98, -117.18) * mm, v(432.37, -113.14) * mm, v(431.56, -108.7) * mm, v(431.56, -104.1) * mm]});
            skFitSpline(sketch, "E334", {"points": [v(431.56, -104.1) * mm, v(431.56, -99.52) * mm, v(432.23, -95.2) * mm, v(433.85, -91.15) * mm]});
            skFitSpline(sketch, "E335", {"points": [v(433.85, -91.15) * mm, v(435.47, -87.1) * mm, v(437.63, -83.6) * mm, v(440.46, -80.63) * mm]});
            skFitSpline(sketch, "E336", {"points": [v(440.46, -80.63) * mm, v(443.16, -77.67) * mm, v(446.4, -75.37) * mm, v(450.17, -73.62) * mm]});
            skFitSpline(sketch, "E337", {"points": [v(450.17, -73.62) * mm, v(453.81, -72) * mm, v(457.86, -71.06) * mm, v(462.17, -71.06) * mm]});
            skFitSpline(sketch, "E338", {"points": [v(462.17, -71.06) * mm, v(467.3, -71.06) * mm, v(471.88, -72.4) * mm, v(476.2, -74.83) * mm]});
            skFitSpline(sketch, "E339", {"points": [v(476.2, -74.83) * mm, v(480.51, -77.26) * mm, v(483.75, -80.64) * mm, v(486.18, -84.95) * mm]});
            skFitSpline(sketch, "E340", {"points": [v(488.88, -84) * mm, v(486.45, -79.15) * mm, v(482.94, -75.24) * mm, v(478.36, -72.54) * mm]});
            skFitSpline(sketch, "E341", {"points": [v(478.36, -72.54) * mm, v(473.77, -69.84) * mm, v(468.5, -68.36) * mm, v(462.58, -68.36) * mm]});
            skFitSpline(sketch, "E342", {"points": [v(528, -68.36) * mm, v(524.63, -68.36) * mm, v(521.53, -68.77) * mm, v(518.56, -69.58) * mm]});
            skFitSpline(sketch, "E343", {"points": [v(518.56, -69.58) * mm, v(515.6, -70.39) * mm, v(512.9, -71.46) * mm, v(510.74, -73.08) * mm]});
            skFitSpline(sketch, "E344", {"points": [v(510.74, -73.08) * mm, v(508.45, -74.7) * mm, v(506.7, -76.86) * mm, v(505.34, -79.28) * mm]});
            skFitSpline(sketch, "E345", {"points": [v(505.34, -79.28) * mm, v(504, -81.71) * mm, v(503.32, -84.68) * mm, v(503.32, -88.2) * mm]});
            skFitSpline(sketch, "E346", {"points": [v(503.32, -88.2) * mm, v(503.32, -91.02) * mm, v(503.73, -93.31) * mm, v(504.67, -95.07) * mm]});
            skFitSpline(sketch, "E347", {"points": [v(504.67, -95.07) * mm, v(505.61, -96.82) * mm, v(506.97, -98.3) * mm, v(508.85, -99.38) * mm]});
            skFitSpline(sketch, "E348", {"points": [v(508.85, -99.38) * mm, v(510.74, -100.6) * mm, v(513.03, -101.54) * mm, v(515.86, -102.35) * mm]});
            skFitSpline(sketch, "E349", {"points": [v(515.86, -102.35) * mm, v(518.56, -103.16) * mm, v(521.93, -103.97) * mm, v(525.7, -104.78) * mm]});
            skFitSpline(sketch, "E350", {"points": [v(525.7, -104.78) * mm, v(529.49, -105.72) * mm, v(533, -106.67) * mm, v(536.1, -107.48) * mm]});
            skFitSpline(sketch, "E351", {"points": [v(536.1, -107.48) * mm, v(539.06, -108.29) * mm, v(541.63, -109.36) * mm, v(543.79, -110.58) * mm]});
            skFitSpline(sketch, "E352", {"points": [v(543.79, -110.58) * mm, v(545.8, -111.8) * mm, v(547.43, -113.27) * mm, v(548.5, -114.9) * mm]});
            skFitSpline(sketch, "E353", {"points": [v(548.5, -114.9) * mm, v(549.58, -116.5) * mm, v(550.13, -118.67) * mm, v(550.13, -121.1) * mm]});
            skFitSpline(sketch, "E354", {"points": [v(550.13, -121.1) * mm, v(550.13, -126.5) * mm, v(547.96, -130.67) * mm, v(543.65, -133.64) * mm]});
            skFitSpline(sketch, "E355", {"points": [v(543.65, -133.64) * mm, v(539.33, -136.6) * mm, v(533.67, -138.1) * mm, v(526.8, -138.1) * mm]});
            skFitSpline(sketch, "E356", {"points": [v(526.8, -138.1) * mm, v(521.67, -138.1) * mm, v(517.22, -137.28) * mm, v(513.3, -135.53) * mm]});
            skFitSpline(sketch, "E357", {"points": [v(513.3, -135.53) * mm, v(509.4, -133.9) * mm, v(505.62, -131.21) * mm, v(502.11, -127.7) * mm]});
            skFitSpline(sketch, "E358", {"points": [v(500.09, -129.46) * mm, v(506.97, -137) * mm, v(515.87, -140.79) * mm, v(526.8, -140.79) * mm]});
            skFitSpline(sketch, "E359", {"points": [v(526.8, -140.79) * mm, v(530.57, -140.79) * mm, v(534.2, -140.38) * mm, v(537.44, -139.44) * mm]});
            skFitSpline(sketch, "E360", {"points": [v(537.44, -139.44) * mm, v(540.68, -138.5) * mm, v(543.38, -137.15) * mm, v(545.67, -135.4) * mm]});
            skFitSpline(sketch, "E361", {"points": [v(545.67, -135.4) * mm, v(547.83, -133.64) * mm, v(549.58, -131.48) * mm, v(550.93, -129.05) * mm]});
            skFitSpline(sketch, "E362", {"points": [v(550.93, -129.05) * mm, v(552.15, -126.63) * mm, v(552.82, -123.8) * mm, v(552.82, -120.7) * mm]});
            skFitSpline(sketch, "E363", {"points": [v(552.82, -120.7) * mm, v(552.82, -117.73) * mm, v(552.15, -115.16) * mm, v(550.93, -113.28) * mm]});
            skFitSpline(sketch, "E364", {"points": [v(550.93, -113.28) * mm, v(549.58, -111.39) * mm, v(547.83, -109.63) * mm, v(545.54, -108.28) * mm]});
            skFitSpline(sketch, "E365", {"points": [v(545.54, -108.28) * mm, v(543.24, -106.94) * mm, v(540.41, -105.86) * mm, v(537.04, -104.91) * mm]});
            skFitSpline(sketch, "E366", {"points": [v(537.04, -104.91) * mm, v(533.67, -104.1) * mm, v(529.9, -103.16) * mm, v(525.85, -102.08) * mm]});
            skFitSpline(sketch, "E367", {"points": [v(525.85, -102.08) * mm, v(522.34, -101.27) * mm, v(519.37, -100.6) * mm, v(516.95, -99.79) * mm]});
            skFitSpline(sketch, "E368", {"points": [v(516.95, -99.79) * mm, v(514.38, -99.11) * mm, v(512.36, -98.3) * mm, v(510.74, -97.22) * mm]});
            skFitSpline(sketch, "E369", {"points": [v(510.74, -97.22) * mm, v(509.12, -96.28) * mm, v(507.91, -95.06) * mm, v(507.1, -93.58) * mm]});
            skFitSpline(sketch, "E370", {"points": [v(507.1, -93.58) * mm, v(506.3, -92.1) * mm, v(506.02, -90.2) * mm, v(506.02, -87.78) * mm]});
            skFitSpline(sketch, "E371", {"points": [v(506.02, -87.78) * mm, v(506.02, -84.81) * mm, v(506.56, -82.39) * mm, v(507.64, -80.23) * mm]});
            skFitSpline(sketch, "E372", {"points": [v(507.64, -80.23) * mm, v(508.72, -78.07) * mm, v(510.34, -76.32) * mm, v(512.36, -74.97) * mm]});
            skFitSpline(sketch, "E373", {"points": [v(512.36, -74.97) * mm, v(514.25, -73.62) * mm, v(516.54, -72.68) * mm, v(519.24, -72) * mm]});
            skFitSpline(sketch, "E374", {"points": [v(519.24, -72) * mm, v(521.8, -71.47) * mm, v(524.5, -71.06) * mm, v(527.47, -71.06) * mm]});
            skFitSpline(sketch, "E375", {"points": [v(527.47, -71.06) * mm, v(531.92, -71.06) * mm, v(536.1, -71.87) * mm, v(540, -73.22) * mm]});
            skFitSpline(sketch, "E376", {"points": [v(540, -73.22) * mm, v(543.79, -74.7) * mm, v(546.61, -76.86) * mm, v(548.37, -79.56) * mm]});
            skFitSpline(sketch, "E377", {"points": [v(550.8, -78.48) * mm, v(549.18, -75.65) * mm, v(546.48, -73.22) * mm, v(542.44, -71.33) * mm]});
            skFitSpline(sketch, "E378", {"points": [v(542.44, -71.33) * mm, v(538.4, -69.44) * mm, v(533.67, -68.36) * mm, v(528, -68.36) * mm]});
            skFitSpline(sketch, "E379", {"points": [v(93.18, -95.2) * mm, v(95.06, -88.19) * mm, v(98.3, -82.66) * mm, v(103.16, -78.61) * mm]});
            skFitSpline(sketch, "E380", {"points": [v(103.16, -78.61) * mm, v(108.02, -74.56) * mm, v(113.68, -72.4) * mm, v(120.42, -72.14) * mm]});
            skFitSpline(sketch, "E381", {"points": [v(120.42, -69.44) * mm, v(119.88, -69.44) * mm, v(119.2, -69.58) * mm, v(118.4, -69.58) * mm]});
            skFitSpline(sketch, "E382", {"points": [v(118.4, -69.58) * mm, v(117.6, -69.58) * mm, v(116.78, -69.71) * mm, v(115.97, -69.71) * mm]});
            skFitSpline(sketch, "E383", {"points": [v(115.97, -69.71) * mm, v(111.38, -70.25) * mm, v(106.94, -72.14) * mm, v(102.89, -75.38) * mm]});
            skFitSpline(sketch, "E384", {"points": [v(102.89, -75.38) * mm, v(98.84, -78.61) * mm, v(95.6, -82.66) * mm, v(93.18, -87.52) * mm]});
            skFitSpline(sketch, "E385", {"points": [v(158.71, -71.06) * mm, v(162.76, -71.06) * mm, v(166.66, -72) * mm, v(170.44, -73.76) * mm]});
            skFitSpline(sketch, "E386", {"points": [v(170.44, -73.76) * mm, v(174.22, -75.65) * mm, v(177.45, -78.07) * mm, v(180.29, -81.04) * mm]});
            skFitSpline(sketch, "E387", {"points": [v(180.29, -81.04) * mm, v(182.98, -84.14) * mm, v(185.28, -87.65) * mm, v(186.9, -91.7) * mm]});
            skFitSpline(sketch, "E388", {"points": [v(186.9, -91.7) * mm, v(188.52, -95.74) * mm, v(189.32, -100.06) * mm, v(189.32, -104.5) * mm]});
            skFitSpline(sketch, "E389", {"points": [v(189.32, -104.5) * mm, v(189.32, -109.1) * mm, v(188.52, -113.4) * mm, v(186.9, -117.46) * mm]});
            skFitSpline(sketch, "E390", {"points": [v(186.9, -117.46) * mm, v(185.28, -121.5) * mm, v(182.99, -125.14) * mm, v(180.15, -128.1) * mm]});
            skFitSpline(sketch, "E391", {"points": [v(180.15, -128.1) * mm, v(177.32, -131.2) * mm, v(174.08, -133.64) * mm, v(170.3, -135.4) * mm]});
            skFitSpline(sketch, "E392", {"points": [v(170.3, -135.4) * mm, v(166.53, -137.28) * mm, v(162.62, -138.1) * mm, v(158.57, -138.1) * mm]});
            skFitSpline(sketch, "E393", {"points": [v(158.57, -138.1) * mm, v(154.26, -138.1) * mm, v(150.35, -137.28) * mm, v(146.7, -135.53) * mm]});
            skFitSpline(sketch, "E394", {"points": [v(146.7, -135.53) * mm, v(142.93, -133.77) * mm, v(139.69, -131.35) * mm, v(137, -128.38) * mm]});
            skFitSpline(sketch, "E395", {"points": [v(137, -128.38) * mm, v(134.3, -125.41) * mm, v(132.14, -121.77) * mm, v(130.52, -117.73) * mm]});
            skFitSpline(sketch, "E396", {"points": [v(130.52, -117.73) * mm, v(128.9, -113.68) * mm, v(128.1, -109.5) * mm, v(128.1, -104.91) * mm]});
            skFitSpline(sketch, "E397", {"points": [v(128.1, -104.91) * mm, v(128.1, -100.33) * mm, v(128.9, -96.01) * mm, v(130.52, -91.97) * mm]});
            skFitSpline(sketch, "E398", {"points": [v(130.52, -91.97) * mm, v(132.14, -87.92) * mm, v(134.3, -84.28) * mm, v(137.13, -81.18) * mm]});
            skFitSpline(sketch, "E399", {"points": [v(137.13, -81.18) * mm, v(139.83, -78.07) * mm, v(143.07, -75.65) * mm, v(146.84, -73.76) * mm]});
            skFitSpline(sketch, "E400", {"points": [v(146.84, -73.76) * mm, v(150.62, -72) * mm, v(154.53, -71.06) * mm, v(158.71, -71.06) * mm]});
            skFitSpline(sketch, "E401", {"points": [v(240.84, -71.06) * mm, v(245.16, -71.06) * mm, v(249.2, -72) * mm, v(252.84, -73.89) * mm]});
            skFitSpline(sketch, "E402", {"points": [v(252.84, -73.89) * mm, v(256.48, -75.78) * mm, v(259.58, -78.34) * mm, v(262.28, -81.45) * mm]});
            skFitSpline(sketch, "E403", {"points": [v(262.28, -81.45) * mm, v(264.98, -84.55) * mm, v(267, -88.05) * mm, v(268.48, -92.1) * mm]});
            skFitSpline(sketch, "E404", {"points": [v(268.48, -92.1) * mm, v(269.83, -96.14) * mm, v(270.65, -100.33) * mm, v(270.65, -104.64) * mm]});
            skFitSpline(sketch, "E405", {"points": [v(270.65, -104.64) * mm, v(270.65, -108.82) * mm, v(269.84, -112.87) * mm, v(268.35, -116.91) * mm]});
            skFitSpline(sketch, "E406", {"points": [v(268.35, -116.91) * mm, v(266.73, -120.96) * mm, v(264.58, -124.47) * mm, v(261.88, -127.57) * mm]});
            skFitSpline(sketch, "E407", {"points": [v(261.88, -127.57) * mm, v(259.18, -130.8) * mm, v(255.8, -133.37) * mm, v(252.03, -135.26) * mm]});
            skFitSpline(sketch, "E408", {"points": [v(252.03, -135.26) * mm, v(248.26, -137.15) * mm, v(244.07, -138.1) * mm, v(239.62, -138.1) * mm]});
            skFitSpline(sketch, "E409", {"points": [v(239.62, -138.1) * mm, v(236.93, -138.1) * mm, v(233.96, -137.55) * mm, v(230.86, -136.47) * mm]});
            skFitSpline(sketch, "E410", {"points": [v(230.86, -136.47) * mm, v(227.62, -135.4) * mm, v(224.79, -133.78) * mm, v(222.09, -131.89) * mm]});
            skFitSpline(sketch, "E411", {"points": [v(222.09, -131.89) * mm, v(219.4, -130) * mm, v(217.1, -127.7) * mm, v(215.21, -125.14) * mm]});
            skFitSpline(sketch, "E412", {"points": [v(215.21, -125.14) * mm, v(213.32, -122.58) * mm, v(212.38, -119.88) * mm, v(212.24, -116.91) * mm]});
            skFitSpline(sketch, "E413", {"points": [v(212.24, -91.42) * mm, v(213.6, -88.73) * mm, v(215.21, -86.16) * mm, v(217.1, -83.74) * mm]});
            skFitSpline(sketch, "E414", {"points": [v(217.1, -83.74) * mm, v(219, -81.3) * mm, v(221, -79.15) * mm, v(223.44, -77.26) * mm]});
            skFitSpline(sketch, "E415", {"points": [v(223.44, -77.26) * mm, v(225.87, -75.37) * mm, v(228.43, -73.9) * mm, v(231.4, -72.81) * mm]});
            skFitSpline(sketch, "E416", {"points": [v(231.4, -72.81) * mm, v(234.36, -71.73) * mm, v(237.47, -71.06) * mm, v(240.84, -71.06) * mm]});
            skFitSpline(sketch, "E417", {"points": [v(319.13, -71.06) * mm, v(323.18, -71.06) * mm, v(327.09, -72) * mm, v(330.86, -73.76) * mm]});
            skFitSpline(sketch, "E418", {"points": [v(330.86, -73.76) * mm, v(334.64, -75.65) * mm, v(337.88, -78.07) * mm, v(340.72, -81.04) * mm]});
            skFitSpline(sketch, "E419", {"points": [v(340.72, -81.04) * mm, v(343.41, -84.14) * mm, v(345.7, -87.65) * mm, v(347.32, -91.7) * mm]});
            skFitSpline(sketch, "E420", {"points": [v(347.32, -91.7) * mm, v(348.94, -95.74) * mm, v(349.75, -100.06) * mm, v(349.75, -104.5) * mm]});
            skFitSpline(sketch, "E421", {"points": [v(349.75, -104.5) * mm, v(349.75, -109.1) * mm, v(348.94, -113.4) * mm, v(347.32, -117.46) * mm]});
            skFitSpline(sketch, "E422", {"points": [v(347.32, -117.46) * mm, v(345.7, -121.5) * mm, v(343.4, -125.14) * mm, v(340.58, -128.1) * mm]});
            skFitSpline(sketch, "E423", {"points": [v(340.58, -128.1) * mm, v(337.74, -131.2) * mm, v(334.5, -133.64) * mm, v(330.73, -135.4) * mm]});
            skFitSpline(sketch, "E424", {"points": [v(330.73, -135.4) * mm, v(326.96, -137.28) * mm, v(323.04, -138.1) * mm, v(319, -138.1) * mm]});
            skFitSpline(sketch, "E425", {"points": [v(319, -138.1) * mm, v(314.68, -138.1) * mm, v(310.77, -137.28) * mm, v(307.13, -135.53) * mm]});
            skFitSpline(sketch, "E426", {"points": [v(307.13, -135.53) * mm, v(303.35, -133.77) * mm, v(300.12, -131.35) * mm, v(297.42, -128.38) * mm]});
            skFitSpline(sketch, "E427", {"points": [v(297.42, -128.38) * mm, v(294.72, -125.41) * mm, v(292.57, -121.77) * mm, v(290.95, -117.73) * mm]});
            skFitSpline(sketch, "E428", {"points": [v(290.95, -117.73) * mm, v(289.33, -113.68) * mm, v(288.52, -109.5) * mm, v(288.52, -104.91) * mm]});
            skFitSpline(sketch, "E429", {"points": [v(288.52, -104.91) * mm, v(288.52, -100.33) * mm, v(289.33, -96.01) * mm, v(290.95, -91.97) * mm]});
            skFitSpline(sketch, "E430", {"points": [v(290.95, -91.97) * mm, v(292.57, -87.92) * mm, v(294.72, -84.28) * mm, v(297.55, -81.18) * mm]});
            skFitSpline(sketch, "E431", {"points": [v(297.55, -81.18) * mm, v(300.25, -78.07) * mm, v(303.49, -75.65) * mm, v(307.27, -73.76) * mm]});
            skFitSpline(sketch, "E432", {"points": [v(307.27, -73.76) * mm, v(311.04, -72) * mm, v(314.95, -71.06) * mm, v(319.13, -71.06) * mm]});
            skSolve(sketch);
        }
        {
            var Q0;
            Q0=makeQuery(id+"F0.imprint","IMPRINT",FACE,{"disambiguationData":[TD([[makeQuery(id+"F0.imprint","IMPRINT",EDGE,{"derivedFrom":sQuery(id+"F0.wireOp",EDGE,"E5")}),-1.0]])]});
            var Q1;
            Q1=makeQuery(id+"F0.imprint","IMPRINT",FACE,{"disambiguationData":[TD([[makeQuery(id+"F0.imprint","IMPRINT",EDGE,{"derivedFrom":sQuery(id+"F0.wireOp",EDGE,"E9")}),-1.0]])]});
            var Q2;
            Q2=makeQuery(id+"F0.imprint","IMPRINT",FACE,{"disambiguationData":[TD([[makeQuery(id+"F0.imprint","IMPRINT",EDGE,{"derivedFrom":sQuery(id+"F0.wireOp",EDGE,"E1")}),-1.0]])]});
            var Q3;
            Q3=makeQuery(id+"F0.imprint","IMPRINT",FACE,{"disambiguationData":[TD([[makeQuery(id+"F0.imprint","IMPRINT",EDGE,{"derivedFrom":sQuery(id+"F0.wireOp",EDGE,"E33")}),-1.0]])]});
            var Q4;
            Q4=makeQuery(id+"F0.imprint","IMPRINT",FACE,{"disambiguationData":[TD([[makeQuery(id+"F0.imprint","IMPRINT",EDGE,{"derivedFrom":sQuery(id+"F0.wireOp",EDGE,"E36")}),1.0]])]});
            var Q5;
            Q5=makeQuery(id+"F0.imprint","IMPRINT",FACE,{"disambiguationData":[TD([[makeQuery(id+"F0.imprint","IMPRINT",EDGE,{"derivedFrom":sQuery(id+"F0.wireOp",EDGE,"E18")}),1.0]])]});
            var Q6;
            Q6=makeQuery(id+"F0.imprint","IMPRINT",FACE,{"disambiguationData":[TD([[makeQuery(id+"F0.imprint","IMPRINT",EDGE,{"derivedFrom":sQuery(id+"F0.wireOp",EDGE,"E23")}),-1.0]])]});
            var Q7;
            Q7=makeQuery(id+"F0.imprint","IMPRINT",FACE,{"disambiguationData":[TD([[makeQuery(id+"F0.imprint","IMPRINT",EDGE,{"derivedFrom":sQuery(id+"F0.wireOp",EDGE,"E24")}),1.0]])]});
            var Q8;
            Q8=makeQuery(id+"F0.imprint","IMPRINT",FACE,{"disambiguationData":[TD([[makeQuery(id+"F0.imprint","IMPRINT",EDGE,{"derivedFrom":sQuery(id+"F0.wireOp",EDGE,"E28")}),1.0]])]});
            var Q9;
            Q9=makeQuery(id+"F0.imprint","IMPRINT",FACE,{"disambiguationData":[TD([[makeQuery(id+"F0.imprint","IMPRINT",EDGE,{"derivedFrom":sQuery(id+"F0.wireOp",EDGE,"E200")}),1.0]])]});
            var Q10;
            Q10=makeQuery(id+"F0.imprint","IMPRINT",FACE,{"disambiguationData":[TD([[makeQuery(id+"F0.imprint","IMPRINT",EDGE,{"derivedFrom":sQuery(id+"F0.wireOp",EDGE,"E42")}),1.0]])]});
            var Q11;
            Q11=makeQuery(id+"F0.imprint","IMPRINT",FACE,{"disambiguationData":[TD([[makeQuery(id+"F0.imprint","IMPRINT",EDGE,{"derivedFrom":sQuery(id+"F0.wireOp",EDGE,"E88")}),1.0]])]});
            var Q12;
            Q12=makeQuery(id+"F0.imprint","IMPRINT",FACE,{"disambiguationData":[TD([[makeQuery(id+"F0.imprint","IMPRINT",EDGE,{"derivedFrom":sQuery(id+"F0.wireOp",EDGE,"E91")}),-1.0]])]});
            var Q13;
            Q13=makeQuery(id+"F0.imprint","IMPRINT",FACE,{"disambiguationData":[TD([[makeQuery(id+"F0.imprint","IMPRINT",EDGE,{"derivedFrom":sQuery(id+"F0.wireOp",EDGE,"E94")}),1.0]])]});
            var Q14;
            Q14=makeQuery(id+"F0.imprint","IMPRINT",FACE,{"disambiguationData":[TD([[makeQuery(id+"F0.imprint","IMPRINT",EDGE,{"derivedFrom":sQuery(id+"F0.wireOp",EDGE,"E282")}),1.0]])]});
            var Q15;
            Q15=makeQuery(id+"F0.imprint","IMPRINT",FACE,{"disambiguationData":[TD([[makeQuery(id+"F0.imprint","IMPRINT",EDGE,{"derivedFrom":sQuery(id+"F0.wireOp",EDGE,"E53")}),1.0]])]});
            var Q16;
            Q16=makeQuery(id+"F0.imprint","IMPRINT",FACE,{"disambiguationData":[TD([[makeQuery(id+"F0.imprint","IMPRINT",EDGE,{"derivedFrom":sQuery(id+"F0.wireOp",EDGE,"E56")}),-1.0]])]});
            var Q17;
            Q17=makeQuery(id+"F0.imprint","IMPRINT",FACE,{"disambiguationData":[TD([[makeQuery(id+"F0.imprint","IMPRINT",EDGE,{"derivedFrom":sQuery(id+"F0.wireOp",EDGE,"E57")}),1.0]])]});
            var Q18;
            Q18=makeQuery(id+"F0.imprint","IMPRINT",FACE,{"disambiguationData":[TD([[makeQuery(id+"F0.imprint","IMPRINT",EDGE,{"derivedFrom":sQuery(id+"F0.wireOp",EDGE,"E298")}),1.0]])]});
            var Q19;
            {var subQ0=sQuery(id+"F0.wireOp",EDGE,"E65");Q19=makeQuery(id+"F0.imprint","IMPRINT",FACE,{"disambiguationData":[TD([[makeQuery(id+"F0.imprint","IMPRINT",EDGE,{"derivedFrom":subQ0}),1.0]])]});}
            var Q20;
            Q20=makeQuery(id+"F0.imprint","IMPRINT",FACE,{"disambiguationData":[TD([[makeQuery(id+"F0.imprint","IMPRINT",EDGE,{"derivedFrom":sQuery(id+"F0.wireOp",EDGE,"E73")}),1.0]])]});
            var Q21;
            Q21=makeQuery(id+"F0.imprint","IMPRINT",FACE,{"disambiguationData":[TD([[makeQuery(id+"F0.imprint","IMPRINT",EDGE,{"derivedFrom":sQuery(id+"F0.wireOp",EDGE,"E72")}),-1.0]])]});
            var Q22;
            Q22=makeQuery(id+"F0.imprint","IMPRINT",FACE,{"disambiguationData":[TD([[makeQuery(id+"F0.imprint","IMPRINT",EDGE,{"derivedFrom":sQuery(id+"F0.wireOp",EDGE,"E98")}),1.0]])]});
            var Q23;
            Q23=makeQuery(id+"F0.imprint","IMPRINT",FACE,{"disambiguationData":[TD([[makeQuery(id+"F0.imprint","IMPRINT",EDGE,{"derivedFrom":sQuery(id+"F0.wireOp",EDGE,"E60")}),1.0]])]});
            var Q24;
            Q24=makeQuery(id+"F0.imprint","IMPRINT",FACE,{"disambiguationData":[TD([[makeQuery(id+"F0.imprint","IMPRINT",EDGE,{"derivedFrom":sQuery(id+"F0.wireOp",EDGE,"E81")}),-1.0]])]});
            var Q25;
            Q25=makeQuery(id+"F0.imprint","IMPRINT",FACE,{"disambiguationData":[TD([[makeQuery(id+"F0.imprint","IMPRINT",EDGE,{"derivedFrom":sQuery(id+"F0.wireOp",EDGE,"E85")}),-1.0]])]});
            extrude(context, id + "F1", {"entities" : qUnion([Q0, Q1, Q2, Q3, Q4, Q5, Q6, Q7, Q8, Q9, Q10, Q11, Q12, Q13, Q14, Q15, Q16, Q17, Q18, Q19, Q20, Q21, Q22, Q23, Q24, Q25]), "depth" : 20 * mm, "offsetDistance" : 25 * mm});
        }
    });
